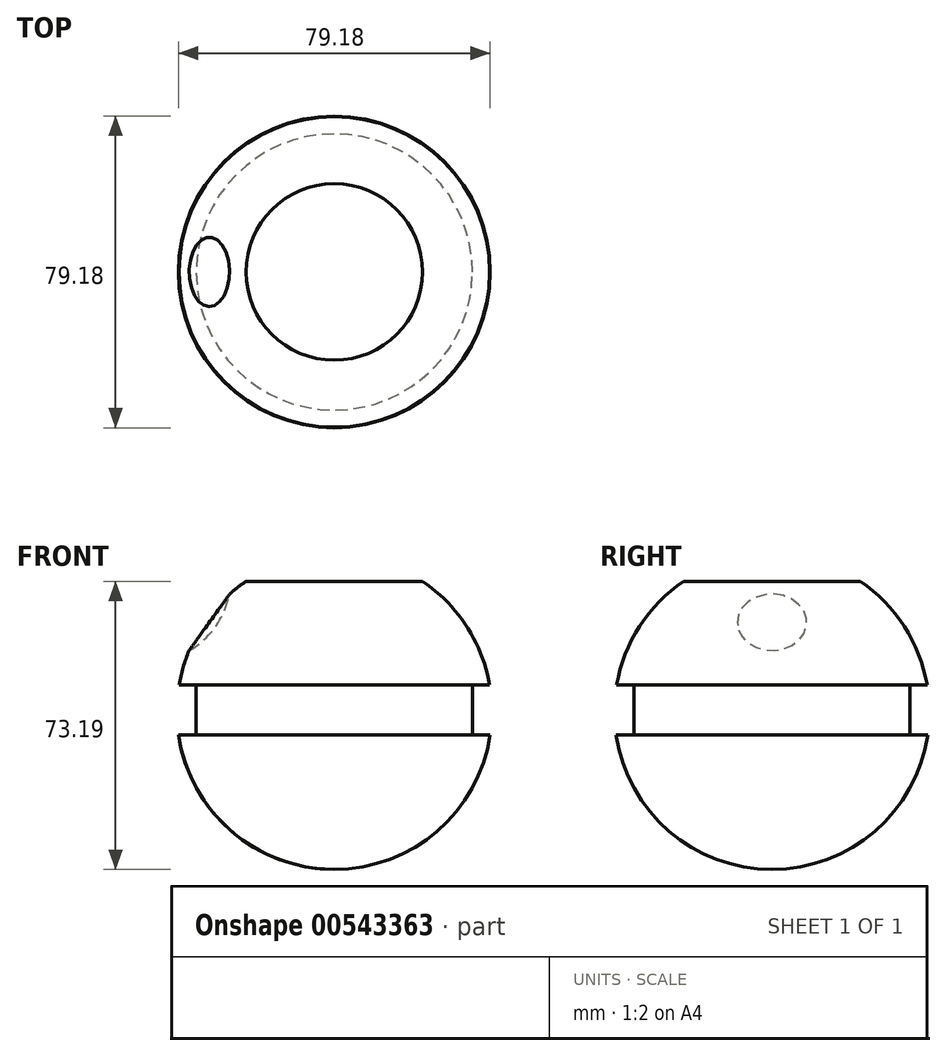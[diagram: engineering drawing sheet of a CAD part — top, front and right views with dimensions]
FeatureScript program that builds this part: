
annotation { "Feature Type Name" : "Feature", "Feature Type Description" : "" }
export const myFeature = defineFeature(function(context is Context, id is Id, definition is map)
    precondition{}
    {
        {
            var Q0;
            Q0=qCreatedBy(makeId("Front.planeOp"),FACE);
            var sketch = newSketch(context, id + "F0", { "sketchPlane" : qUnion([Q0])});
            skLineSegment(sketch, "E0", {"start": v(32.34, 29.8) * mm, "end": v(32.34, 29.8) * mm});
            skArc(sketch, "E1", {"start": v(0, -40.03) * mm, "mid": v(26.13, -30.32) * mm, "end": v(39.59, -5.92) * mm});
            skLineSegment(sketch, "E2", {"start": v(0, 53.17) * mm, "end": v(0, -47.79) * mm, "construction": true});
            skLineSegment(sketch, "E3", {"start": v(0, 40.03) * mm, "end": v(0, -40.03) * mm});
            skLineSegment(sketch, "E4.bottom", {"start": v(35.08, 6.8) * mm, "end": v(39.44, 6.8) * mm});
            skLineSegment(sketch, "E4.top", {"start": v(35.08, -5.92) * mm, "end": v(39.59, -5.92) * mm});
            skLineSegment(sketch, "E4.left", {"start": v(35.08, 6.8) * mm, "end": v(35.08, -5.92) * mm});
            skArc(sketch, "E5.trimOffspring", {"start": v(39.44, 6.8) * mm, "mid": v(33.62, 21.72) * mm, "end": v(22.42, 33.16) * mm});
            skLineSegment(sketch, "E6", {"start": v(0, 33.16) * mm, "end": v(22.42, 33.16) * mm});
            skSolve(sketch);
        }
        {
            var Q0;
            Q0=makeQuery(id+"F0.imprint","IMPRINT",FACE,{"disambiguationData":[TD([[makeQuery(id+"F0.imprint","IMPRINT",EDGE,{"derivedFrom":sQuery(id+"F0.wireOp",EDGE,"E1")}),1.0]])]});
            var Q1;
            Q1 = qSketchRegion(id + "F0", true);
            var Q2;
            Q2=sQuery(id+"F0.wireOp",EDGE,"E2");
            revolve(context, id + "F1", {"entities" : qUnion([Q0, Q1]), "axis" : qUnion([Q2]), "revolveType" : RevolveType.FULL});
        }
        {
            var Q0;
            Q0=qCreatedBy(makeId("Front.planeOp"),FACE);
            var sketch = newSketch(context, id + "F2", { "sketchPlane" : qUnion([Q0])});
            skArc(sketch, "E7", {"start": v(-47.5, 12.73) * mm, "mid": v(-26.2, 34.05) * mm, "end": v(-47.5, 55.36) * mm});
            skLineSegment(sketch, "E8", {"start": v(-47.5, 55.36) * mm, "end": v(-47.5, 12.73) * mm});
            skSolve(sketch);
        }
        {
            var Q0;
            Q0 = qSketchRegion(id + "F2", true);
            var Q1;
            Q1=sQuery(id+"F2.wireOp",EDGE,"E8");
            revolve(context, id + "F3", {"operationType" : NewBodyOperationType.REMOVE, "entities" : qUnion([Q0]), "axis" : qUnion([Q1]), "revolveType" : RevolveType.FULL, "oppositeDirection" : true});
        }
    });
